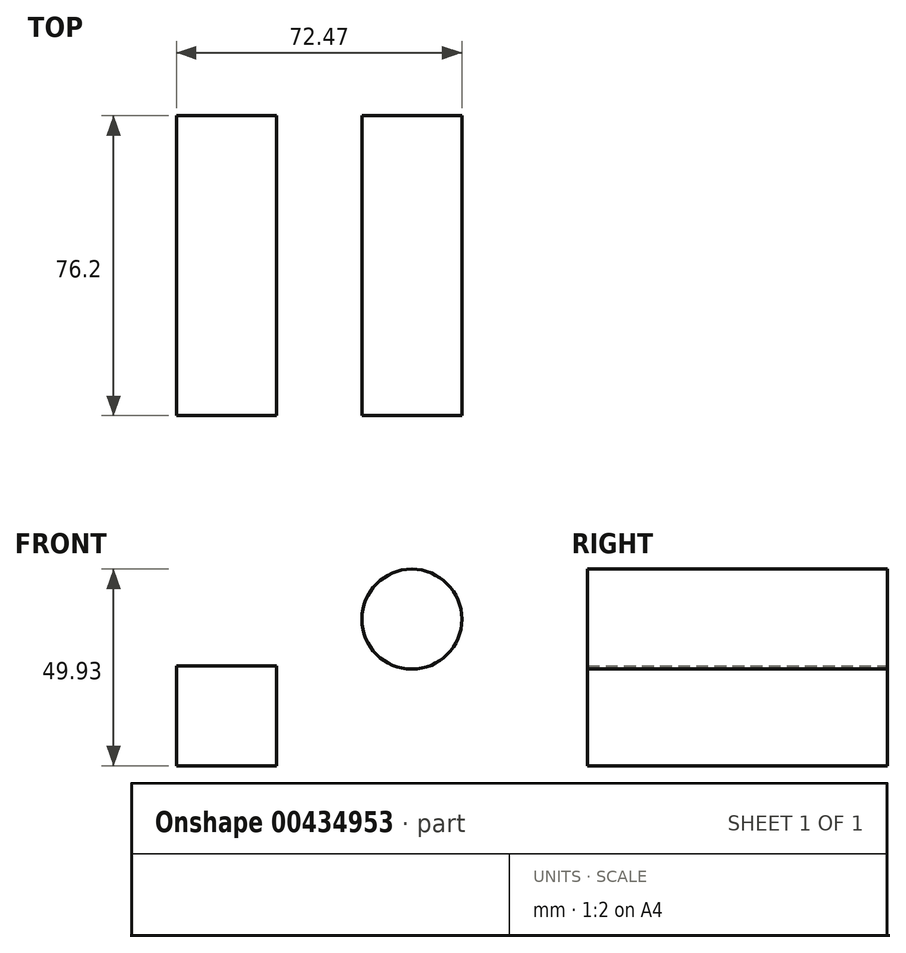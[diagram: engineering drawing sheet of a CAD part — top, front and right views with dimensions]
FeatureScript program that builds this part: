
annotation { "Feature Type Name" : "Feature", "Feature Type Description" : "" }
export const myFeature = defineFeature(function(context is Context, id is Id, definition is map)
    precondition{}
    {
        {
            var Q0;
            Q0=qCreatedBy(makeId("Front.planeOp"),FACE);
            var sketch = newSketch(context, id + "F0", { "sketchPlane" : qUnion([Q0])});
            skLineSegment(sketch, "E0.bottom", {"start": v(-41.25, 4.78) * mm, "end": v(-15.85, 4.78) * mm});
            skLineSegment(sketch, "E0.top", {"start": v(-41.25, -20.62) * mm, "end": v(-15.85, -20.62) * mm});
            skLineSegment(sketch, "E0.left", {"start": v(-41.25, 4.78) * mm, "end": v(-41.25, -20.62) * mm});
            skLineSegment(sketch, "E0.right", {"start": v(-15.85, 4.78) * mm, "end": v(-15.85, -20.62) * mm});
            skCircle(sketch, "E1", {"center": v(18.52, 16.61) * mm, "radius": 12.7 * mm});
            skSolve(sketch);
        }
        {
            var Q0;
            Q0=makeQuery(id+"F0.imprint","IMPRINT",FACE,{"disambiguationData":[TD([[makeQuery(id+"F0.imprint","IMPRINT",EDGE,{"derivedFrom":sQuery(id+"F0.wireOp",EDGE,"E1")}),1.0]])]});
            var Q1;
            Q1=makeQuery(id+"F0.imprint","IMPRINT",FACE,{"disambiguationData":[TD([[makeQuery(id+"F0.imprint","IMPRINT",EDGE,{"derivedFrom":sQuery(id+"F0.wireOp",EDGE,"E0.bottom")}),-1.0]])]});
            extrude(context, id + "F1", {"entities" : qUnion([Q0, Q1]), "depth" : 76.2 * mm});
        }
    });
